# Revit family: SH-446-20w
name_source: partatom
category: Lighting Fixtures
revit_build: Autodesk Revit 2017 (Build: 20160225_1515(x64)
units: mm (PartAtom-declared; Revit-internal decimal feet)

## family parameters
Always vertical = No
Cut with Voids When Loaded = No
Light Source = No
OmniClass Number = 23.80.70.00
OmniClass Title = Lighting
Part Type = Normal
Room Calculation Point = No
Round Connector Dimension = Use Diameter
Shared = Yes
Work Plane-Based = Yes

## types (4) — shared parameters
Body Material = Aluminum
Default Elevation = 121.9 cm
Diameter = 6.5 cm
Flicker = Free Flicker
Height = 21.4 cm
IP = IP20
Lamp = LED
Manufacturer = SHOA
Model = SH-446
Protection Class = Class I
Type medule = COB
URL = https://www.shoaco.com
Voltage/Frequency = 230V/50HZ
Website = www.shoaco.com
color rendering index(CRI) = 80<
consumption current = 0 A
wattage = 20 W

## per-type parameters (varying)
| type | 3000K | 4000K | Body color | color temperature |
| Sh-446(black color-3000K-LED) | Yes | No | black color | 3000K |
| Sh-446(black color-4000K-LED) | No | Yes | black color | 4000K |
| Sh-446(White color-4000K-LED) | No | Yes | White color1 | 4000K |
| Sh-446(White color-3000K-LED) | Yes | No | White color1 | 3000K |

## geometry (parser evidence)
native form markers: Sweep x11
no freeform markers — native parametric forms only
